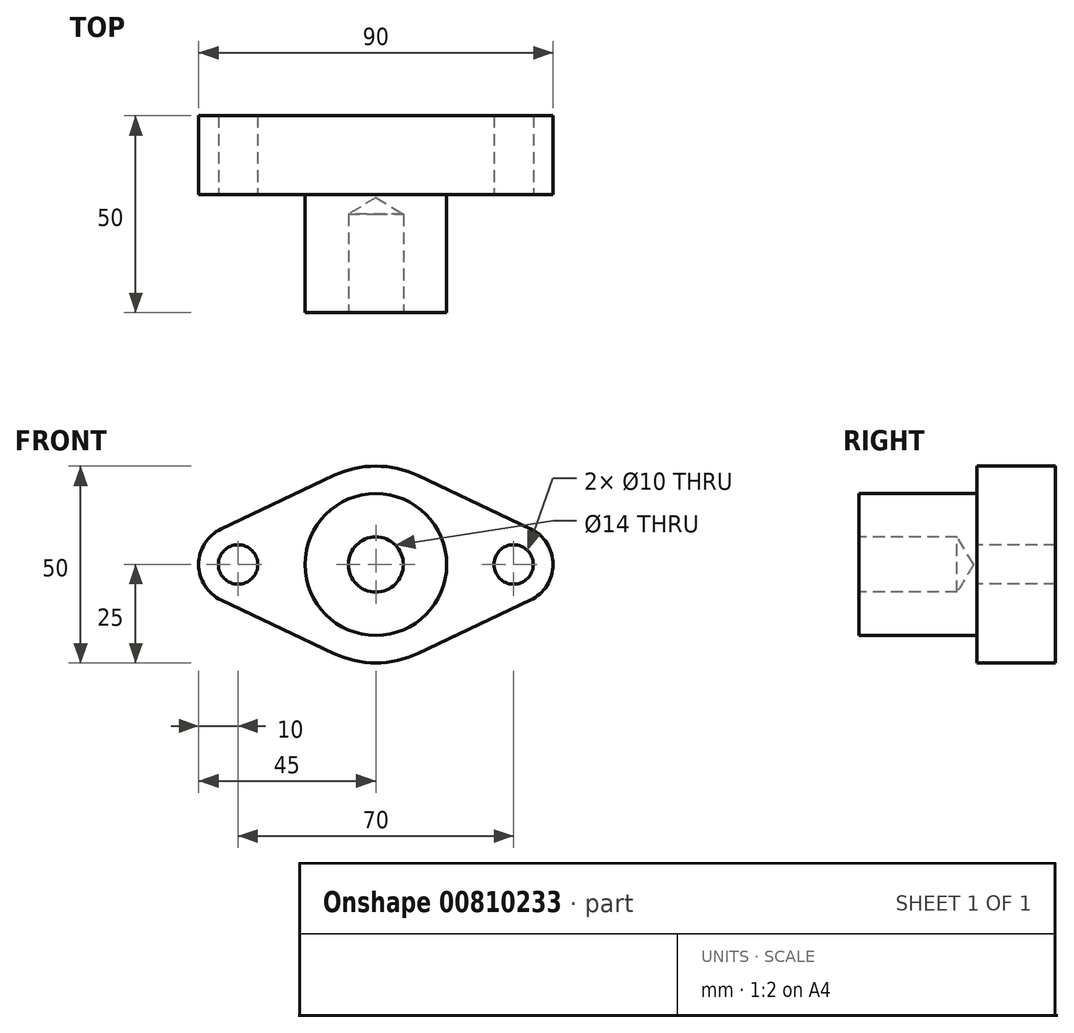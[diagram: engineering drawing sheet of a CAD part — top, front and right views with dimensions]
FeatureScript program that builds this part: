
annotation { "Feature Type Name" : "Feature", "Feature Type Description" : "" }
export const myFeature = defineFeature(function(context is Context, id is Id, definition is map)
    precondition{}
    {
        {
            var Q0;
            Q0=qCreatedBy(makeId("Front.planeOp"),FACE);
            var sketch = newSketch(context, id + "F0", { "sketchPlane" : qUnion([Q0])});
            skPoint(sketch, "E0", {"position": v(35, 0) * mm});
            skPoint(sketch, "E1", {"position": v(-35, 0) * mm});
            skLineSegment(sketch, "E2", {"start": v(-58.33, 0) * mm, "end": v(0, 27.67) * mm});
            skLineSegment(sketch, "E3", {"start": v(0, 27.67) * mm, "end": v(58.33, 0) * mm});
            skLineSegment(sketch, "E4", {"start": v(58.33, 0) * mm, "end": v(0, -27.67) * mm});
            skLineSegment(sketch, "E5", {"start": v(0, -27.67) * mm, "end": v(-58.33, 0) * mm});
            skPoint(sketch, "E6", {"position": v(-58.33, 0) * mm});
            skPoint(sketch, "E7", {"position": v(0, -27.67) * mm});
            skPoint(sketch, "E8", {"position": v(0, 27.67) * mm});
            skSolve(sketch);
        }
        {
            var Q0;
            Q0=makeQuery(id+"F0.imprint","IMPRINT",FACE,{"disambiguationData":[TD([[makeQuery(id+"F0.imprint","IMPRINT",EDGE,{"derivedFrom":sQuery(id+"F0.wireOp",EDGE,"E2")}),-1.0]])]});
            extrude(context, id + "F1", {"entities" : qUnion([Q0]), "oppositeDirection" : true, "depth" : 20 * mm, "offsetDistance" : 25 * mm});
        }
        {
            var Q0;
            Q0=makeQuery(id+"F1.opExtrude","SWEPT_EDGE",EDGE,{"disambiguationData":[OSD([sQuery(id+"F0.wireOp",EDGE,"E4"),sQuery(id+"F0.wireOp",EDGE,"E5")])]});
            var Q1;
            Q1=makeQuery(id+"F1.opExtrude","SWEPT_EDGE",EDGE,{"disambiguationData":[OSD([sQuery(id+"F0.wireOp",EDGE,"E2"),sQuery(id+"F0.wireOp",EDGE,"E3")])]});
            fillet(context, id + "F2", {"entities" : qUnion([Q0, Q1]), "radius" : 25 * mm, "tangentPropagation" : true, "allowEdgeOverflow" : false});
        }
        {
            var Q0;
            Q0=makeQuery(id+"F1.opExtrude","SWEPT_EDGE",EDGE,{"disambiguationData":[OSD([sQuery(id+"F0.wireOp",EDGE,"E2"),sQuery(id+"F0.wireOp",EDGE,"E5")])]});
            var Q1;
            Q1=makeQuery(id+"F1.opExtrude","SWEPT_EDGE",EDGE,{"disambiguationData":[OSD([sQuery(id+"F0.wireOp",EDGE,"E3"),sQuery(id+"F0.wireOp",EDGE,"E4")])]});
            fillet(context, id + "F3", {"entities" : qUnion([Q0, Q1]), "radius" : 10 * mm, "tangentPropagation" : true, "allowEdgeOverflow" : false});
        }
        {
            var Q0;
            Q0=makeQuery(id+"F0.imprint","IMPRINT",FACE,{"disambiguationData":[TD([[makeQuery(id+"F0.imprint","IMPRINT",EDGE,{"derivedFrom":sQuery(id+"F0.wireOp",EDGE,"E2")}),-1.0]])]});
            var sketch = newSketch(context, id + "F4", { "sketchPlane" : qUnion([Q0])});
            skCircle(sketch, "E9", {"center": v(0, 0) * mm, "radius": 18 * mm});
            skSolve(sketch);
        }
        {
            var Q0;
            Q0=makeQuery(id+"F4.imprint","IMPRINT",FACE,{"disambiguationData":[TD([[makeQuery(id+"F4.imprint","IMPRINT",EDGE,{"derivedFrom":sQuery(id+"F4.wireOp",EDGE,"E9")}),1.0]])]});
            extrude(context, id + "F5", {"entities" : qUnion([Q0]), "operationType" : NewBodyOperationType.ADD, "depth" : 30 * mm, "offsetDistance" : 25 * mm});
        }
        {
            var Q0;
            Q0=makeQuery(id+"F5.opExtrude","CAP_FACE",FACE,{"disambiguationData":[OSD([sQuery(id+"F4.wireOp",EDGE,"E9")])],"isStart":false});
            var sketch = newSketch(context, id + "F6", { "sketchPlane" : qUnion([Q0])});
            skPoint(sketch, "E10", {"position": v(0, 0) * mm});
            skSolve(sketch);
        }
        {
            var Q0;
            Q0=sQuery(id+"F0.wireOp",VERTEX,"E1");
            var Q1;
            Q1=sQuery(id+"F0.wireOp",VERTEX,"E0");
            var Q2;
            Q2=makeQuery(id+"F1.opExtrude","SWEPT_BODY",BODY,{"disambiguationData":[OSD([sQuery(id+"F0.wireOp",EDGE,"E2"),sQuery(id+"F0.wireOp",EDGE,"E3"),sQuery(id+"F0.wireOp",EDGE,"E4"),sQuery(id+"F0.wireOp",EDGE,"E5")])]});
            hole(context, id + "F7", {"style" : HoleStyle.SIMPLE, "endStyle" : HoleEndStyle.THROUGH, "holeDiameter" : 10 * mm, "majorDiameter" : 5 * mm, "isTappedThrough" : true, "tappedDepth" : 12 * mm, "tapClearance" : 3, "locations" : qUnion([Q0, Q1]), "scope" : qUnion([Q2])});
        }
        {
            var Q0;
            Q0=sQuery(id+"F6.wireOp",VERTEX,"E10");
            var Q1;
            Q1=makeQuery(id+"F1.opExtrude","SWEPT_BODY",BODY,{"disambiguationData":[OSD([sQuery(id+"F0.wireOp",EDGE,"E2"),sQuery(id+"F0.wireOp",EDGE,"E3"),sQuery(id+"F0.wireOp",EDGE,"E4"),sQuery(id+"F0.wireOp",EDGE,"E5")])]});
            hole(context, id + "F8", {"style" : HoleStyle.SIMPLE, "endStyle" : HoleEndStyle.BLIND, "standardTappedOrClearance" : lookupTablePath({ "standard" : "ISO", "engagement" : "75%", "pitch" : "2 mm", "size" : "M16", "type" : "Tapped" }), "standardBlindInLast" : lookupTablePath({ "standard" : "ISO", "engagement" : "75%", "pitch" : "2 mm", "size" : "M16", "type" : "Tapped" }), "holeDiameter" : 14 * mm, "majorDiameter" : 16 * mm, "showTappedDepth" : true, "holeDepth" : 25 * mm, "isTappedThrough" : true, "tappedDepth" : 21 * mm, "tapClearance" : 2, "locations" : qUnion([Q0]), "scope" : qUnion([Q1])});
        }
    });
